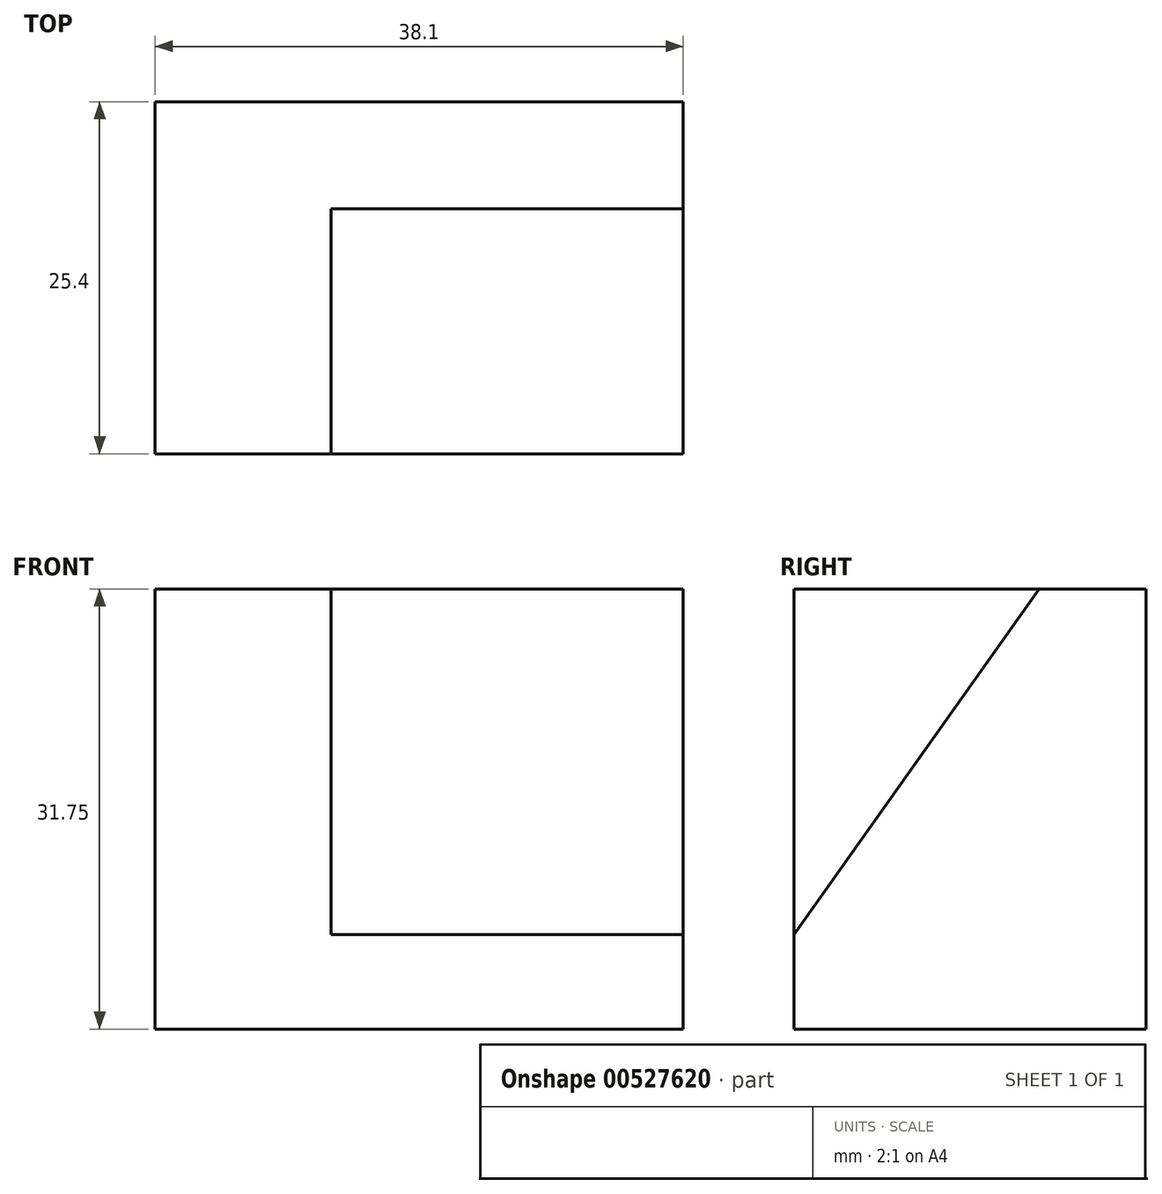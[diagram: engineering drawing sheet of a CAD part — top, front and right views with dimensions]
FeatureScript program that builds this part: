
annotation { "Feature Type Name" : "Feature", "Feature Type Description" : "" }
export const myFeature = defineFeature(function(context is Context, id is Id, definition is map)
    precondition{}
    {
        {
            var Q0;
            Q0=qCreatedBy(makeId("Right.planeOp"),FACE);
            var sketch = newSketch(context, id + "F0", { "sketchPlane" : qUnion([Q0])});
            skLineSegment(sketch, "E0", {"start": v(0, 0) * mm, "end": v(25.4, 0) * mm});
            skLineSegment(sketch, "E1", {"start": v(25.4, 0) * mm, "end": v(25.4, 31.75) * mm});
            skLineSegment(sketch, "E2", {"start": v(25.4, 31.75) * mm, "end": v(0, 31.75) * mm});
            skLineSegment(sketch, "E3", {"start": v(0, 31.75) * mm, "end": v(0, 0) * mm});
            skSolve(sketch);
        }
        {
            var Q0;
            Q0=makeQuery(id+"F0.imprint","IMPRINT",FACE,{"disambiguationData":[TD([[makeQuery(id+"F0.imprint","IMPRINT",EDGE,{"derivedFrom":sQuery(id+"F0.wireOp",EDGE,"E0")}),1.0]])]});
            extrude(context, id + "F1", {"entities" : qUnion([Q0]), "depth" : 38.1 * mm, "offsetDistance" : 25.4 * mm});
        }
        {
            var Q0;
            Q0=makeQuery(id+"F1.opExtrude","CAP_FACE",FACE,{"disambiguationData":[OSD([sQuery(id+"F0.wireOp",EDGE,"E0"),sQuery(id+"F0.wireOp",EDGE,"E1"),sQuery(id+"F0.wireOp",EDGE,"E2"),sQuery(id+"F0.wireOp",EDGE,"E3")])],"isStart":false});
            var sketch = newSketch(context, id + "F2", { "sketchPlane" : qUnion([Q0])});
            skLineSegment(sketch, "E4", {"start": v(17.68, 31.75) * mm, "end": v(0, 6.82) * mm});
            skLineSegment(sketch, "E5", {"start": v(17.68, 31.75) * mm, "end": v(0, 31.75) * mm});
            skLineSegment(sketch, "E6", {"start": v(0, 31.75) * mm, "end": v(0, 6.82) * mm});
            skSolve(sketch);
        }
        {
            var Q0;
            Q0=makeQuery(id+"F2.imprint","IMPRINT",FACE,{"disambiguationData":[TD([[makeQuery(id+"F2.imprint","IMPRINT",EDGE,{"derivedFrom":sQuery(id+"F2.wireOp",EDGE,"E4")}),-1.0]])]});
            extrude(context, id + "F3", {"entities" : qUnion([Q0]), "operationType" : NewBodyOperationType.REMOVE, "oppositeDirection" : true, "depth" : 25.4 * mm, "offsetDistance" : 25.4 * mm});
        }
    });
